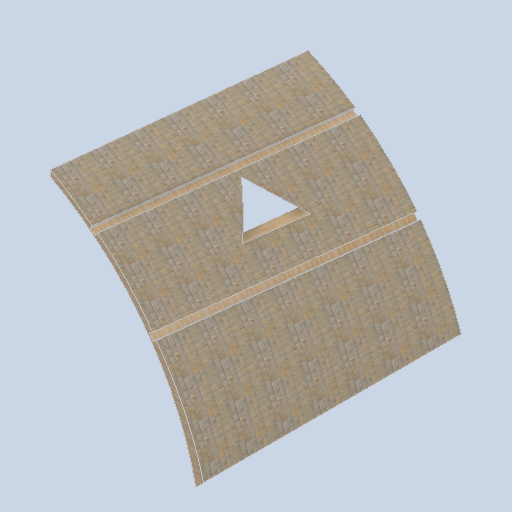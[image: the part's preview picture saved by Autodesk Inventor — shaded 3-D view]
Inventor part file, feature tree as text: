
AUTODESK INVENTOR PART (.ipt)
format: ipt  version: 2024.2 (Build 282272000, 272)  size: 357,888 bytes
history: native  units: in
note: dims shown in document units (in); Inventor stores cm internally (conversion verified against a paired STEP export)
features: other x3, sketch x2, plane x2
ambient origin geometry x8: Origin, YZ Plane, XZ Plane, XY Plane, X Axis, Y Axis, Z Axis, Center Point
bodies: Solid1 (feature_tree)
feature tree (7):
  other  "panel_block_02.ipt"
  other  "Solid1::panel_block_02.ipt"
  other  "TaggingFeature1"
  sketch  "Sketch1"  dims[d0=0.3937in]
  sketch  "Sketch2"
  plane  "Work Plane1"
  plane  "Work Plane2"
